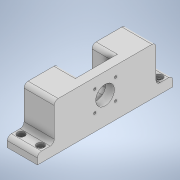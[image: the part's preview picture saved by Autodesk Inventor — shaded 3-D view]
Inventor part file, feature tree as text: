
AUTODESK INVENTOR PART (.ipt)
format: ipt  version: 2020 (Build 240168000, 168)  size: 240,128 bytes
history: native  units: mm
features: extrude x5, sketch x2, other x1, mirror x1
ambient origin geometry x8: Origin, YZ Plane, XZ Plane, XY Plane, X Axis, Y Axis, Z Axis, Center Point
bodies: Body1 (feature_tree)
feature tree (9):
  other  "Bryła1"
  sketch  "Szkic1"
  extrude  "Wyciągnięcie proste1"  Depth=28.0mm
  extrude  "Wyciągnięcie proste2"  Depth=11.0mm
  extrude  "Wyciągnięcie proste4"  Depth=40.0mm
  sketch  "Szkic2"
  extrude  "Wyciągnięcie proste5"  Depth=20.0mm
  extrude  "Wyciągnięcie proste6"  Depth=60.0mm
  mirror  "Odbij1"
